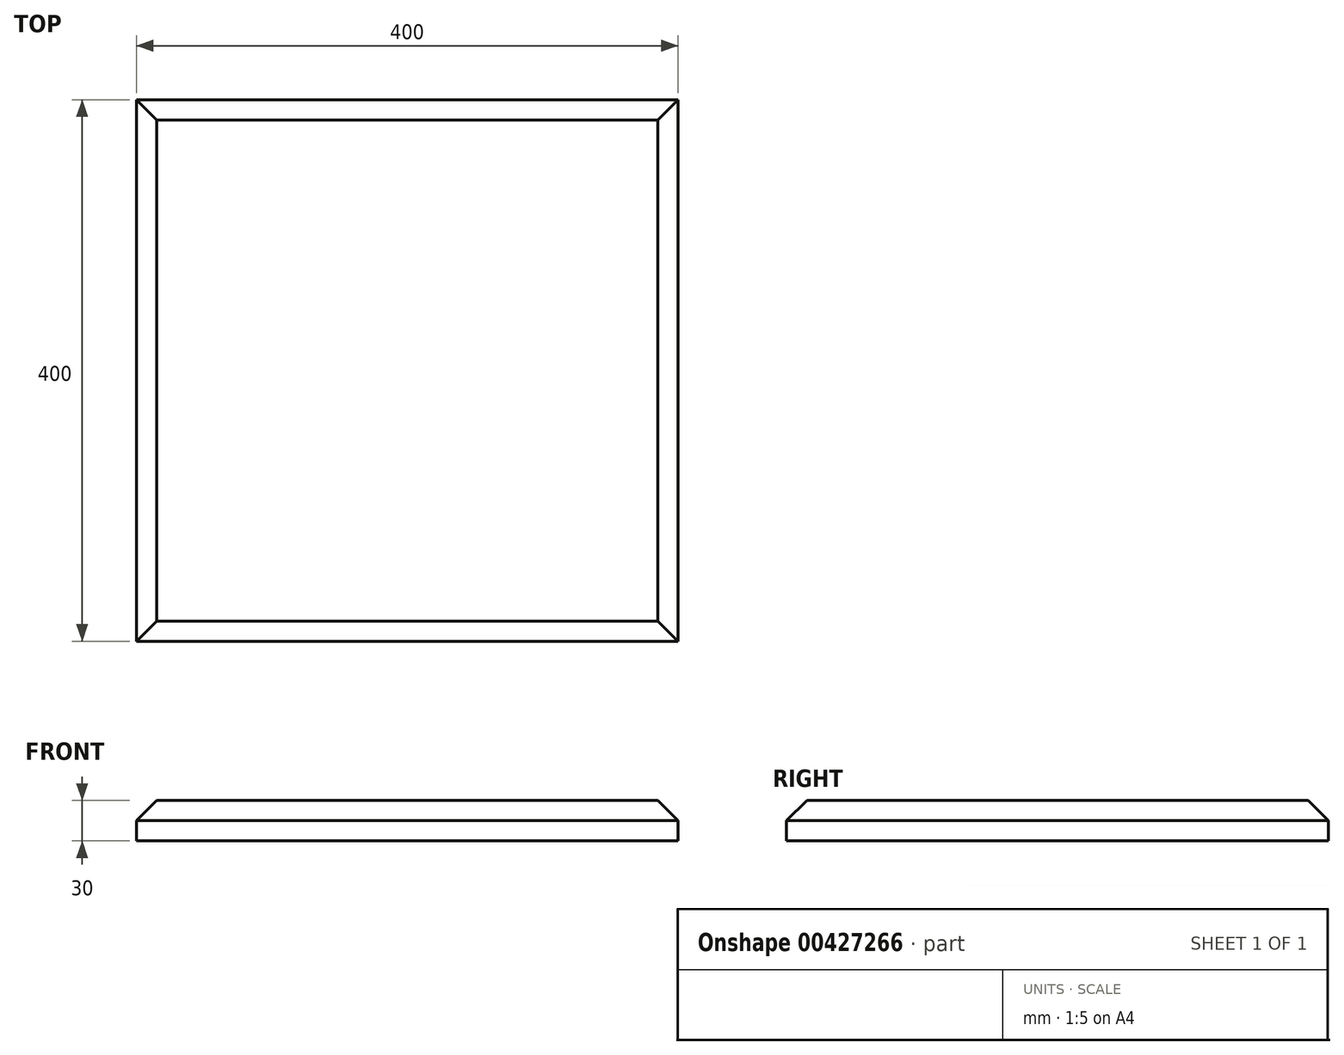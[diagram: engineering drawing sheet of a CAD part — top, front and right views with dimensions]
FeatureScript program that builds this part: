
annotation { "Feature Type Name" : "Feature", "Feature Type Description" : "" }
export const myFeature = defineFeature(function(context is Context, id is Id, definition is map)
    precondition{}
    {
        {
            var Q0;
            Q0=qCreatedBy(makeId("Top.planeOp"),FACE);
            var sketch = newSketch(context, id + "F0", { "sketchPlane" : qUnion([Q0])});
            skLineSegment(sketch, "E0.bottom", {"start": v(200, -200) * mm, "end": v(-200, -200) * mm});
            skLineSegment(sketch, "E0.top", {"start": v(200, 200) * mm, "end": v(-200, 200) * mm});
            skLineSegment(sketch, "E0.left", {"start": v(200, -200) * mm, "end": v(200, 200) * mm});
            skLineSegment(sketch, "E0.right", {"start": v(-200, -200) * mm, "end": v(-200, 200) * mm});
            skPoint(sketch, "E0.middle", {"position": v(0, 0) * mm});
            skSolve(sketch);
        }
        {
            var Q0;
            Q0=makeQuery(id+"F0.imprint","IMPRINT",FACE,{"disambiguationData":[TD([[makeQuery(id+"F0.imprint","IMPRINT",EDGE,{"derivedFrom":sQuery(id+"F0.wireOp",EDGE,"E0.bottom")}),-1.0]])]});
            extrude(context, id + "F1", {"entities" : qUnion([Q0]), "depth" : 30 * mm, "offsetDistance" : 25 * mm});
        }
        {
            var Q0;
            Q0=makeQuery(id+"F1.opExtrude","CAP_FACE",FACE,{"disambiguationData":[OSD([sQuery(id+"F0.wireOp",EDGE,"E0.bottom"),sQuery(id+"F0.wireOp",EDGE,"E0.top"),sQuery(id+"F0.wireOp",EDGE,"E0.left"),sQuery(id+"F0.wireOp",EDGE,"E0.right")])],"isStart":false});
            chamfer(context, id + "F2", {"entities" : qUnion([Q0]), "width" : 15 * mm, "tangentPropagation" : true});
        }
    });
